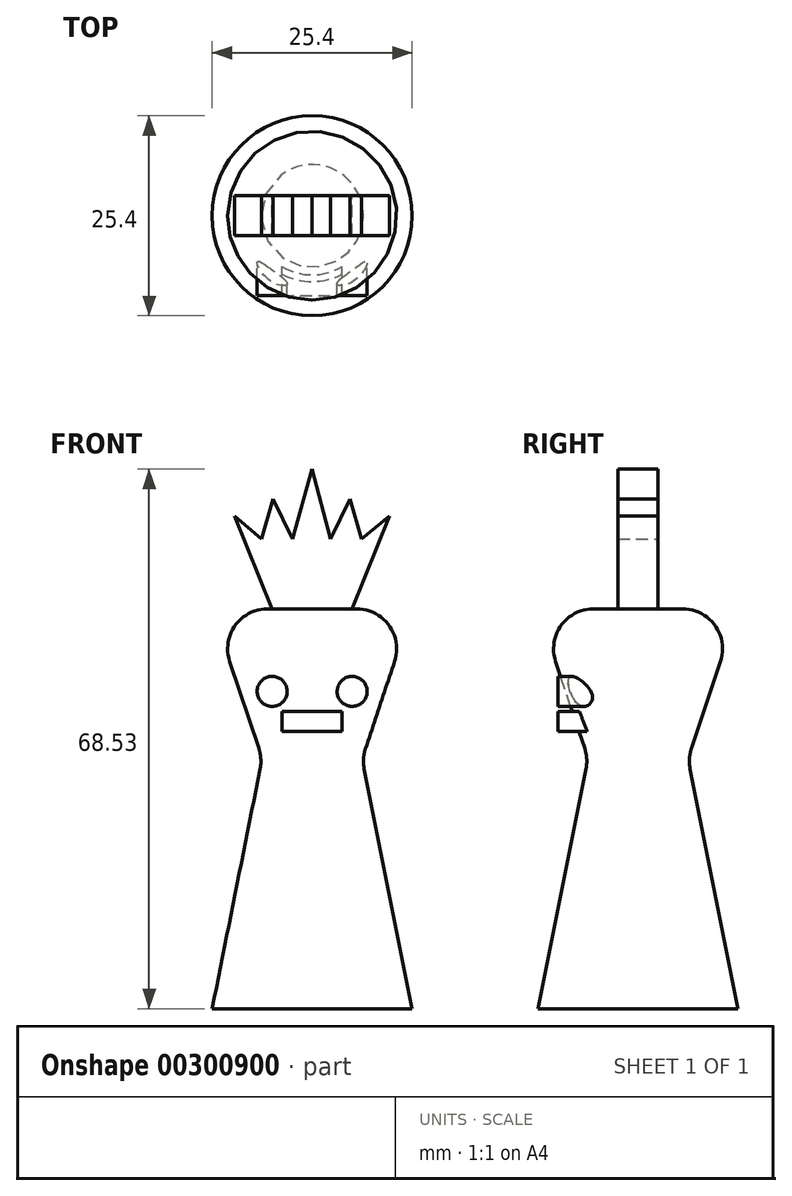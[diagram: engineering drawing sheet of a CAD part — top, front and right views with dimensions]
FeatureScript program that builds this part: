
annotation { "Feature Type Name" : "Feature", "Feature Type Description" : "" }
export const myFeature = defineFeature(function(context is Context, id is Id, definition is map)
    precondition{}
    {
        {
            var Q0;
            Q0=qCreatedBy(makeId("Front.planeOp"),FACE);
            var sketch = newSketch(context, id + "F0", { "sketchPlane" : qUnion([Q0])});
            skLineSegment(sketch, "E0", {"start": v(0, 0) * mm, "end": v(25.4, 0) * mm});
            skLineSegment(sketch, "E1", {"start": v(25.4, 0) * mm, "end": v(19.05, 31.75) * mm});
            skLineSegment(sketch, "E2", {"start": v(19.05, 31.75) * mm, "end": v(25.4, 50.8) * mm});
            skLineSegment(sketch, "E3", {"start": v(25.4, 50.8) * mm, "end": v(0, 50.8) * mm});
            skLineSegment(sketch, "E4", {"start": v(0, 50.8) * mm, "end": v(6.35, 31.75) * mm});
            skLineSegment(sketch, "E5", {"start": v(6.35, 31.75) * mm, "end": v(0, 0) * mm});
            skLineSegment(sketch, "E6", {"start": v(19.05, 31.75) * mm, "end": v(6.35, 31.75) * mm, "construction": true});
            skLineSegment(sketch, "E7", {"start": v(25.4, 50.8) * mm, "end": v(25.4, 0) * mm, "construction": true});
            skLineSegment(sketch, "E8", {"start": v(12.7, 50.8) * mm, "end": v(12.7, 0) * mm});
            skPoint(sketch, "E9", {"position": v(12.7, 31.75) * mm});
            skSolve(sketch);
        }
        {
            var Q0;
            {var subQ3=sQuery(id+"F0.wireOp",EDGE,"E1");Q0=makeQuery(id+"F0.imprint","IMPRINT",FACE,{"disambiguationData":[TD([[makeQuery(id+"F0.imprint","IMPRINT",EDGE,{"derivedFrom":subQ3}),1.0]])]});}
            var Q1;
            Q1=sQuery(id+"F0.wireOp",EDGE,"E8");
            revolve(context, id + "F1", {"entities" : qUnion([Q0]), "axis" : qUnion([Q1]), "revolveType" : RevolveType.FULL});
        }
        {
            var Q0;
            Q0=makeQuery(id+"F1.opRevolve","SWEPT_EDGE",EDGE,{"disambiguationData":[OSD([sQuery(id+"F0.wireOp",EDGE,"E2"),sQuery(id+"F0.wireOp",EDGE,"E3")])]});
            var Q1;
            Q1=makeQuery(id+"F1.opRevolve","SWEPT_EDGE",EDGE,{"disambiguationData":[OSD([sQuery(id+"F0.wireOp",EDGE,"E1"),sQuery(id+"F0.wireOp",EDGE,"E2")])]});
            fillet(context, id + "F2", {"entities" : qUnion([Q0, Q1]), "radius" : 5.08 * mm, "tangentPropagation" : true, "allowEdgeOverflow" : false});
        }
        {
            var Q0;
            Q0=qCreatedBy(makeId("Front.planeOp"),FACE);
            var sketch = newSketch(context, id + "F3", { "sketchPlane" : qUnion([Q0])});
            skLineSegment(sketch, "E10", {"start": v(7.62, 50.8) * mm, "end": v(17.78, 50.8) * mm});
            skLineSegment(sketch, "E11", {"start": v(17.78, 50.8) * mm, "end": v(22.55, 62.57) * mm});
            skLineSegment(sketch, "E12", {"start": v(22.55, 62.57) * mm, "end": v(18.94, 59.64) * mm});
            skLineSegment(sketch, "E13", {"start": v(18.94, 59.64) * mm, "end": v(17.49, 64.72) * mm});
            skLineSegment(sketch, "E14", {"start": v(17.49, 64.72) * mm, "end": v(15, 59.64) * mm});
            skLineSegment(sketch, "E15", {"start": v(15, 59.64) * mm, "end": v(12.7, 68.53) * mm});
            skLineSegment(sketch, "E16", {"start": v(12.7, 68.53) * mm, "end": v(10.19, 59.64) * mm});
            skLineSegment(sketch, "E17", {"start": v(10.19, 59.64) * mm, "end": v(7.7, 64.72) * mm});
            skLineSegment(sketch, "E18", {"start": v(7.7, 64.72) * mm, "end": v(6.25, 59.64) * mm});
            skLineSegment(sketch, "E19", {"start": v(6.25, 59.64) * mm, "end": v(2.85, 62.57) * mm});
            skLineSegment(sketch, "E20", {"start": v(2.85, 62.57) * mm, "end": v(7.62, 50.8) * mm});
            skPoint(sketch, "E21", {"position": v(12.7, 50.8) * mm});
            skLineSegment(sketch, "E22", {"start": v(4.04, 59.64) * mm, "end": v(21.36, 59.64) * mm, "construction": true});
            skLineSegment(sketch, "E23", {"start": v(12.7, 68.53) * mm, "end": v(12.7, 59.64) * mm, "construction": true});
            skLineSegment(sketch, "E24", {"start": v(7.7, 64.72) * mm, "end": v(17.49, 64.72) * mm, "construction": true});
            skLineSegment(sketch, "E25", {"start": v(2.85, 62.57) * mm, "end": v(22.55, 62.57) * mm, "construction": true});
            skSolve(sketch);
        }
        {
            var Q0;
            Q0=makeQuery(id+"F3.imprint","IMPRINT",FACE,{"disambiguationData":[TD([[makeQuery(id+"F3.imprint","IMPRINT",EDGE,{"derivedFrom":sQuery(id+"F3.wireOp",EDGE,"E10")}),1.0]])]});
            extrude(context, id + "F4", {"entities" : qUnion([Q0]), "operationType" : NewBodyOperationType.ADD, "endBound" : BoundingType.SYMMETRIC, "depth" : 5.08 * mm});
        }
        {
            var Q0;
            Q0=qCreatedBy(makeId("Front.planeOp"),FACE);
            var sketch = newSketch(context, id + "F5", { "sketchPlane" : qUnion([Q0])});
            skCircle(sketch, "E26", {"center": v(7.62, 40.3) * mm, "radius": 1.9 * mm});
            skCircle(sketch, "E27", {"center": v(17.78, 40.3) * mm, "radius": 1.9 * mm});
            skLineSegment(sketch, "E28.bottom", {"start": v(8.89, 37.76) * mm, "end": v(16.5, 37.76) * mm});
            skLineSegment(sketch, "E28.top", {"start": v(8.89, 35.22) * mm, "end": v(16.5, 35.22) * mm});
            skLineSegment(sketch, "E28.left", {"start": v(8.89, 37.76) * mm, "end": v(8.89, 35.22) * mm});
            skLineSegment(sketch, "E28.right", {"start": v(16.5, 37.76) * mm, "end": v(16.5, 35.22) * mm});
            skLineSegment(sketch, "E29", {"start": v(7.62, 40.3) * mm, "end": v(17.78, 40.3) * mm, "construction": true});
            skLineSegment(sketch, "E30", {"start": v(12.7, 40.3) * mm, "end": v(12.7, 44.11) * mm, "construction": true});
            skSolve(sketch);
        }
        {
            var Q0;
            Q0 = qSketchRegion(id + "F5", true);
            extrude(context, id + "F6", {"entities" : qUnion([Q0]), "operationType" : NewBodyOperationType.ADD, "depth" : 10.16 * mm});
        }
    });
